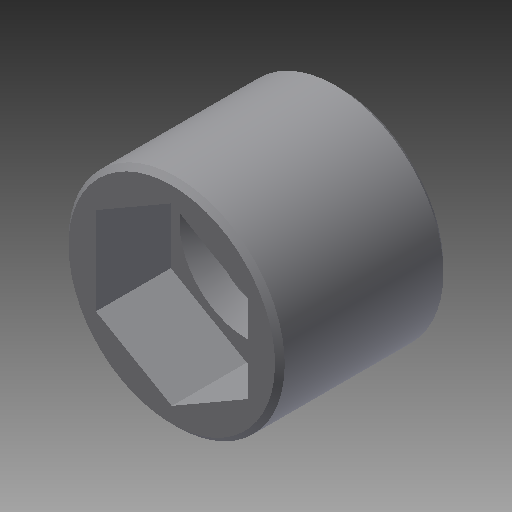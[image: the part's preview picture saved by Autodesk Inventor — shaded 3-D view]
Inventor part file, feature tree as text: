
AUTODESK INVENTOR PART (.ipt)
format: ipt  version: 2019.4 (Build 234330000, 330)  size: 143,360 bytes
history: native  units: in
note: dims shown in document units (in); Inventor stores cm internally (conversion verified against a paired STEP export)
features: other x7, sketch x2, revolve x1, thread x1, extrude x1
ambient origin geometry x8: Origin, YZ Plane, XZ Plane, XY Plane, X Axis, Y Axis, Z Axis, Center Point
bodies: Solid1 (feature_tree)
feature tree (12):
  revolve  "Revolution1"  [1 undecoded]
  thread  "Thread1"  [1 undecoded]
  extrude  "Extrusion1"  [1 undecoded]
  other  "screw_XY"
  other  "screw_YZ"
  other  "screw_ZX"
  other  "screw_X"
  other  "screw_Y"
  other  "screw_Z"
  other  "screw_Center"
  sketch  "Sketch_1"  dims[d0=360.0deg d1=0.0622in d2=0.0in d3=0.077in d4=0.0in]
  sketch  "Sketch_3"  dims[d5=0.0in]
note: 3 required parameter values undecoded (feature->parameter linkage not recoverable at this tier; creation-order binding heuristic only, values carry confidence <= 0.55)